# Revit family: DLCPCC
name_source: partatom
category: Communication Devices
revit_build: Autodesk Revit 2014 (Build: 20130308_1515(x64)
units: mm (PartAtom-declared; Revit-internal decimal feet)

## types (1)
- DLCPCC
    Assembly Code = D5090
    Black = Paint - Hubbell - Carbon Black
    Certifications = ETL/UL 916
    Default Elevation = 48 "
    Description = Hubbell Controls' DLCPCC is the ideal system for providing indoor, outdoor,
or skylight control of lighting circuits based on daylight. The DLCPCC lighting
controller automatically switches a dry contact in response to changes in natural
light levels. The DLCPCC provides a maintained single pole, double throw “Form
C” relay output to drive electrically-held contactors or relays, or inputs to Building
Automation Systems. The low voltage controller requires a remotely mounted
photoconductive (PC) sensor (sold separately).
    Features = Adjustable on/off set points
• Dual power unit input: 24VAC or 24VDC
• Flexible control options
• Input time delay
• Two set points available for separate on and off levels
• Five-year limited warranty
• Low voltage device: 24 Vdc
    Gray = Paint - Hubbell - Gray Smooth
    Height = 4.5 "
    Manufacturer = Hubbell Control Solutions
    Metal = Gold
    Model = DLCPCC
    Product Documentation Link = https://hubbellcdn.com
    Product Page URL = https://www.hubbell.com
    Type Comments = Photocell Controller
    URL = https://www.hubbell.com
    Warranty = 5-Years Warranty
    Width = 2 "

## geometry (parser evidence)
native form markers: Sweep x1
no freeform markers — native parametric forms only
